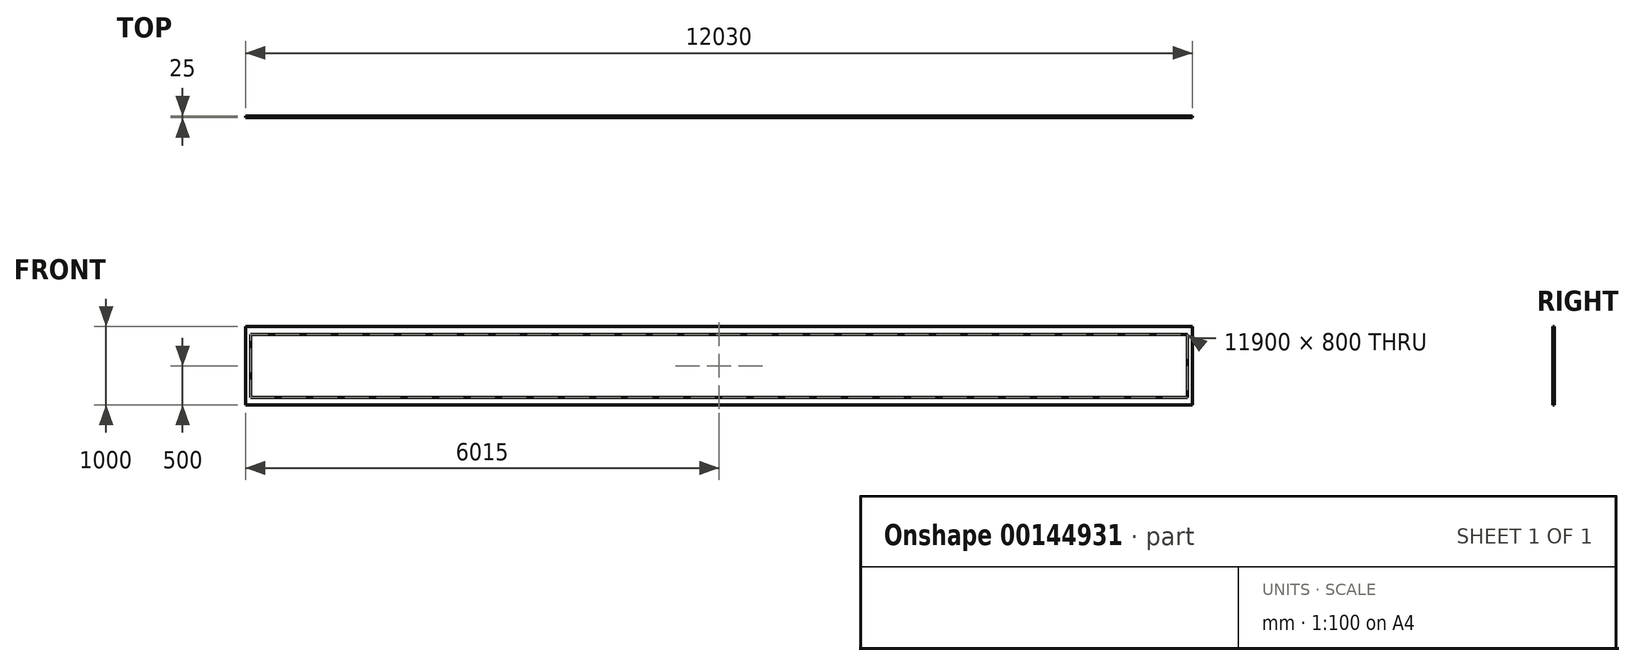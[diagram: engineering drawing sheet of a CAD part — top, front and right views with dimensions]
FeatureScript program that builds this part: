
annotation { "Feature Type Name" : "Feature", "Feature Type Description" : "" }
export const myFeature = defineFeature(function(context is Context, id is Id, definition is map)
    precondition{}
    {
        {
            var Q0;
            Q0=qCreatedBy(makeId("Front.planeOp"),FACE);
            var sketch = newSketch(context, id + "F0", { "sketchPlane" : qUnion([Q0])});
            skLineSegment(sketch, "E0.bottom", {"start": v(6015, -500) * mm, "end": v(-6015, -500) * mm});
            skLineSegment(sketch, "E0.top", {"start": v(6015, 500) * mm, "end": v(-6015, 500) * mm});
            skLineSegment(sketch, "E0.left", {"start": v(6015, -500) * mm, "end": v(6015, 500) * mm});
            skLineSegment(sketch, "E0.right", {"start": v(-6015, -500) * mm, "end": v(-6015, 500) * mm});
            skPoint(sketch, "E0.middle", {"position": v(0, 0) * mm});
            skSolve(sketch);
        }
        {
            var Q0;
            Q0=makeQuery(id+"F0.imprint","IMPRINT",FACE,{"disambiguationData":[TD([[makeQuery(id+"F0.imprint","IMPRINT",EDGE,{"derivedFrom":sQuery(id+"F0.wireOp",EDGE,"E0.bottom")}),-1.0]])]});
            extrude(context, id + "F2", {"entities" : qUnion([Q0]), "depth" : 25 * mm});
        }
        {
            var Q0;
            Q0=makeQuery(id+"F2.opExtrude","CAP_FACE",FACE,{"disambiguationData":[OSD([sQuery(id+"F0.wireOp",EDGE,"E0.bottom"),sQuery(id+"F0.wireOp",EDGE,"E0.top"),sQuery(id+"F0.wireOp",EDGE,"E0.left"),sQuery(id+"F0.wireOp",EDGE,"E0.right")])],"isStart":false});
            var sketch = newSketch(context, id + "F1", { "sketchPlane" : qUnion([Q0])});
            skLineSegment(sketch, "E1.bottom", {"start": v(5950, 400) * mm, "end": v(-5950, 400) * mm});
            skLineSegment(sketch, "E1.top", {"start": v(5950, -400) * mm, "end": v(-5950, -400) * mm});
            skLineSegment(sketch, "E1.left", {"start": v(5950, 400) * mm, "end": v(5950, -400) * mm});
            skLineSegment(sketch, "E1.right", {"start": v(-5950, 400) * mm, "end": v(-5950, -400) * mm});
            skPoint(sketch, "E1.middle", {"position": v(0, 0) * mm});
            skSolve(sketch);
        }
        {
            var Q0;
            Q0=makeQuery(id+"F1.imprint","IMPRINT",FACE,{"disambiguationData":[TD([[makeQuery(id+"F1.imprint","IMPRINT",EDGE,{"derivedFrom":sQuery(id+"F1.wireOp",EDGE,"E1.bottom")}),1.0]])]});
            extrude(context, id + "F3", {"entities" : qUnion([Q0]), "operationType" : NewBodyOperationType.REMOVE, "endBound" : BoundingType.THROUGH_ALL, "oppositeDirection" : true, "depth" : 25 * mm});
        }
    });
